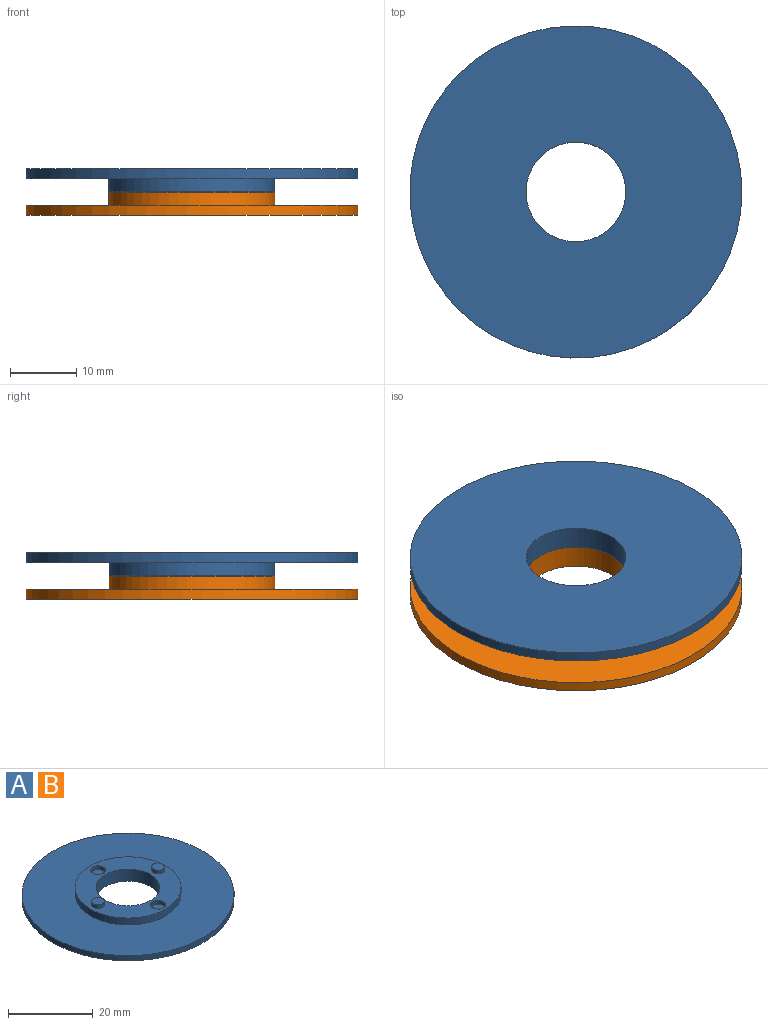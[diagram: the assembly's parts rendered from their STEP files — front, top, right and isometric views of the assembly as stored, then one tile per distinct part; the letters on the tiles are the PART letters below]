
ASSEMBLY  parts=2 mates=1
PART A: 14 faces, bbox 50x50x4.5 mm
  f0: cylinder r=7.5mm len=15mm, axis (0,0,-1), area 164.9mm2, adj f3,f5
  f1: cylinder r=25mm len=50mm, axis (0,0,-1), area 235.6mm2, adj f2,f3
  f2: plane 50x50mm, normal (0,0,1), area 1472.6mm2, adj f1,f4
  f3: plane 50x50mm, normal (0,0,-1), area 1786.8mm2, adj f0,f1
  f4: cylinder r=12.5mm len=25mm, axis (0,0,-1), area 157.1mm2, adj f2,f5
  f5: plane 25x25mm, normal (0,0,1), area 280.8mm2, adj f0,f4,f6,f8,f10,f12
  f6: cylinder r=1.5mm len=3mm, axis (0,0,-1), area 9.4mm2, adj f5,f7
  f7: plane 3x3mm, normal (0,0,1), area 7.1mm2, adj f6
  f8: cylinder r=1.5mm len=3mm, axis (0,0,-1), area 9.4mm2, adj f5,f9
  f9: plane 3x3mm, normal (0,0,1), area 7.1mm2, adj f8
  f10: cylinder r=1.75mm len=3.5mm, axis (0,0,1), area 12.1mm2, adj f5,f11
  f11: plane 3.5x3.5mm, normal (0,0,1), area 9.6mm2, adj f10
  f12: cylinder r=1.75mm len=3.5mm, axis (0,0,1), area 12.1mm2, adj f5,f13
  f13: plane 3.5x3.5mm, normal (0,0,1), area 9.6mm2, adj f12
PART B: same geometry as A
PLACE A rot(axis=(1,0,0),180deg) t=(0.1,-9.8,-49.35)mm
PLACE B t=(0.1,-9.8,-56.35)mm
MATE revolute A.f4 <-> B.f0  axis (0,0,-1) through (0.1,-9.8,-52.85)mm
